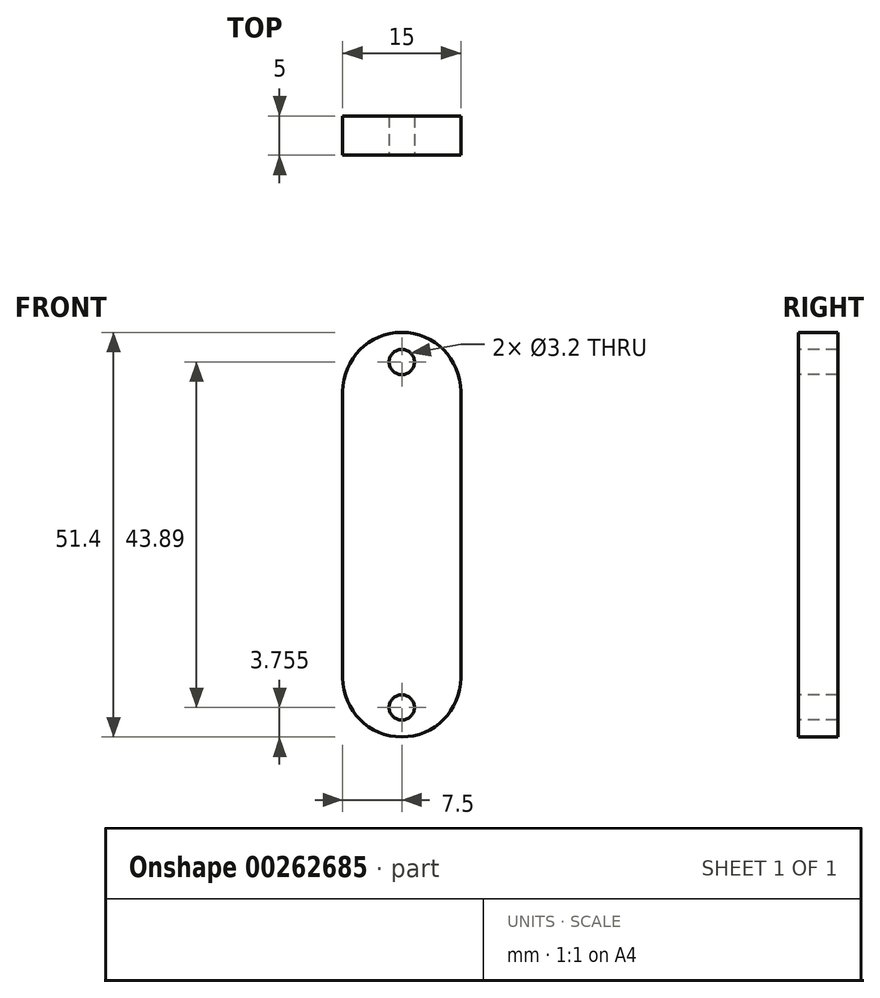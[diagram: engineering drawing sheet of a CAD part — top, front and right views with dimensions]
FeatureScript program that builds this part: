
annotation { "Feature Type Name" : "Feature", "Feature Type Description" : "" }
export const myFeature = defineFeature(function(context is Context, id is Id, definition is map)
    precondition{}
    {
        {
            var Q0;
            Q0=qCreatedBy(makeId("Front.planeOp"),FACE);
            var sketch = newSketch(context, id + "F0", { "sketchPlane" : qUnion([Q0])});
            skLineSegment(sketch, "E0.bottom", {"start": v(7.5, -18.2) * mm, "end": v(-7.5, -18.2) * mm});
            skLineSegment(sketch, "E0.top", {"start": v(7.5, 18.2) * mm, "end": v(-7.5, 18.2) * mm});
            skLineSegment(sketch, "E0.left", {"start": v(7.5, -18.2) * mm, "end": v(7.5, 18.2) * mm});
            skLineSegment(sketch, "E0.right", {"start": v(-7.5, -18.2) * mm, "end": v(-7.5, 18.2) * mm});
            skPoint(sketch, "E0.middle", {"position": v(0, 0) * mm});
            skArc(sketch, "E1", {"start": v(7.5, 18.2) * mm, "mid": v(0, 25.7) * mm, "end": v(-7.5, 18.2) * mm});
            skArc(sketch, "E2", {"start": v(-7.5, -18.2) * mm, "mid": v(0, -25.7) * mm, "end": v(7.5, -18.2) * mm});
            skCircle(sketch, "E3", {"center": v(0, 21.94) * mm, "radius": 1.6 * mm});
            skCircle(sketch, "E4", {"center": v(0, -21.94) * mm, "radius": 1.6 * mm});
            skSolve(sketch);
        }
        {
            var Q0;
            Q0=makeQuery(id+"F0.imprint","IMPRINT",FACE,{"disambiguationData":[TD([[makeQuery(id+"F0.imprint","IMPRINT",EDGE,{"derivedFrom":sQuery(id+"F0.wireOp",EDGE,"E0.top")}),-1.0]])]});
            var Q1;
            Q1=makeQuery(id+"F0.imprint","IMPRINT",FACE,{"disambiguationData":[TD([[makeQuery(id+"F0.imprint","IMPRINT",EDGE,{"derivedFrom":sQuery(id+"F0.wireOp",EDGE,"E0.bottom")}),-1.0]])]});
            var Q2;
            Q2=makeQuery(id+"F0.imprint","IMPRINT",FACE,{"disambiguationData":[TD([[makeQuery(id+"F0.imprint","IMPRINT",EDGE,{"derivedFrom":sQuery(id+"F0.wireOp",EDGE,"E0.bottom")}),1.0]])]});
            extrude(context, id + "F1", {"entities" : qUnion([Q0, Q1, Q2]), "oppositeDirection" : true, "depth" : 5 * mm});
        }
    });
